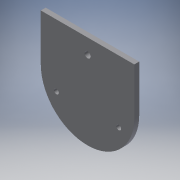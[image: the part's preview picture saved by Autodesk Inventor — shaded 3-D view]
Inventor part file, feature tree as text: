
AUTODESK INVENTOR PART (.ipt)
format: ipt  version: 2016 (Build 200138000, 138)  size: 146,432 bytes
history: native  units: in
note: dims shown in document units (in); Inventor stores cm internally (conversion verified against a paired STEP export)
features: reference x5, extrude x3, sketch x3, plane x1, projected_geometry x1
ambient origin geometry x8: Origin, YZ Plane, XZ Plane, XY Plane, X Axis, Y Axis, Z Axis, Center Point
bodies: Solid1 (feature_tree)
feature tree (13):
  extrude  "Extrusion1"  Depth=3.0in
  plane  "Work Plane1"
  extrude  "Extrusion2"  Depth=0.1575in TaperAngle=0.0deg
  extrude  "Extrusion3"  Depth=0.1575in
  sketch  "Sketch1"  dims[d0=1.0in d1=3.0in]
  reference  "Reference1"
  reference  "Reference2"
  sketch  "Sketch2"  dims[d2=0.1575in d3=0.0in d5=0.1575in d6=0.0in]
  reference  "Reference3"
  sketch  "Sketch3"  dims[d7=1.0in d8=2.0in d9=0.1575in d10=0.1575in d11=1.0in d12=0.0in d13=0.0197in d14=0.197in]
  reference  "Reference4"
  reference  "Reference5"
  projected_geometry  "Projected Loop1"
